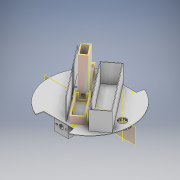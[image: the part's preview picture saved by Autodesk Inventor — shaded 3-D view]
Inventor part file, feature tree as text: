
AUTODESK INVENTOR PART (.ipt)
format: ipt  version: 2020 (Build 240168000, 168)  size: 485,376 bytes
history: native  units: mm
features: other x7, sketch x6, plane x1
ambient origin geometry x8: Origin, YZ Plane, XZ Plane, XY Plane, X Axis, Y Axis, Z Axis, Center Point
bodies: Solid1 (feature_tree)
feature tree (14):
  other  "Donja_konstrinkcija_s_drop_mehanizmom_v.2.0.iam"
  other  "KonstrukcijaDonjiDio_v.1.1.ipt:1"
  other  "DropMechanism_v.2.0.ipt:1"
  sketch  "Sketch2"  dims[d0=10.0mm]
  sketch  "Sketch30"
  sketch  "Sketch31"
  sketch  "Sketch37"
  plane  "Work Plane1"
  other  "Work Axis1"
  other  "Work Axis2"
  sketch  "Sketch3"
  sketch  "Sketch4"
  other  "Srf1"
  other  "Srf1::Derived"
